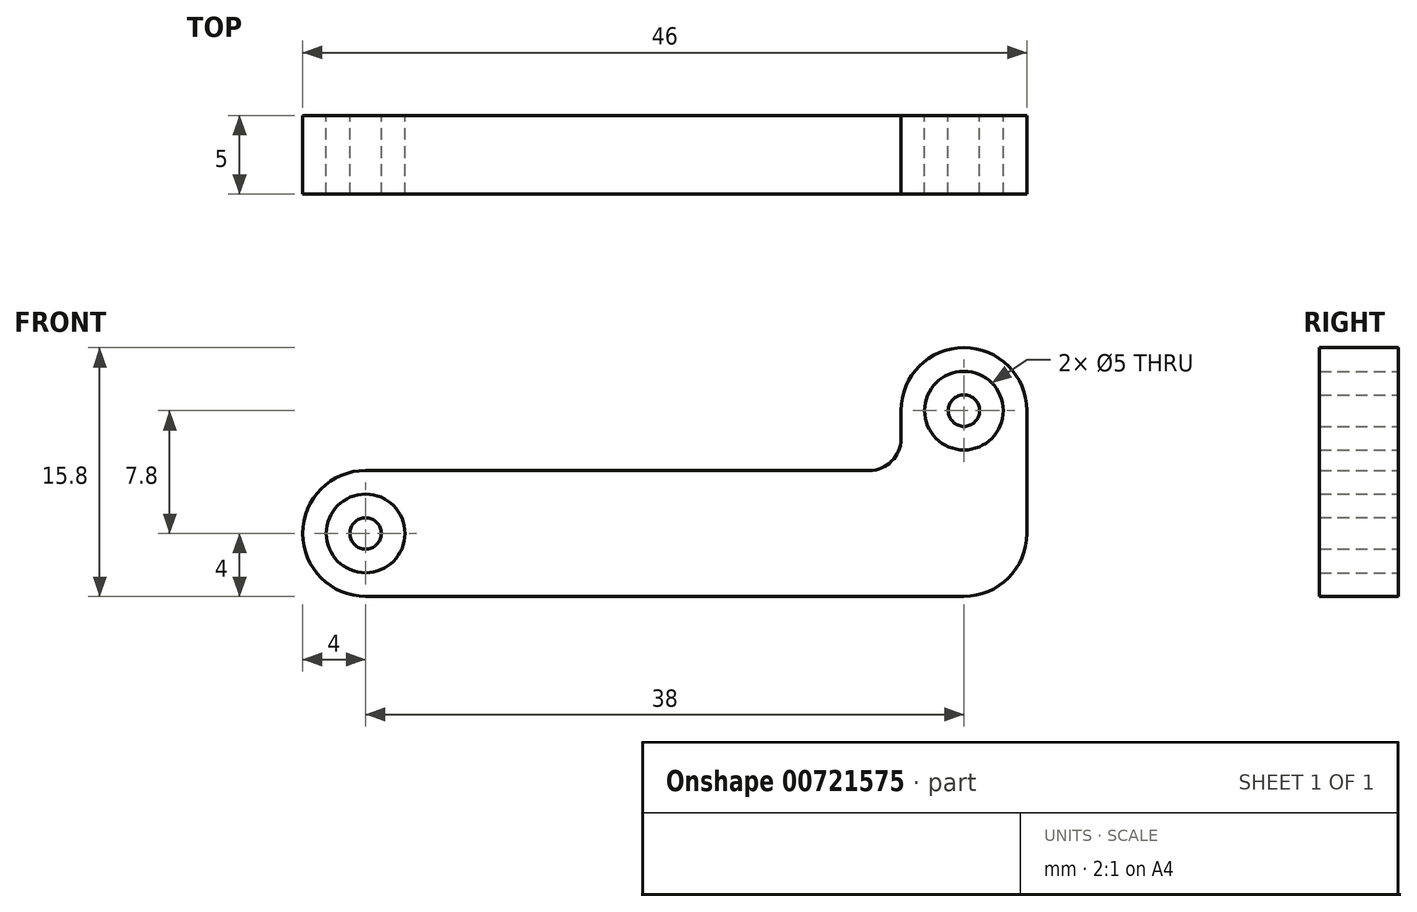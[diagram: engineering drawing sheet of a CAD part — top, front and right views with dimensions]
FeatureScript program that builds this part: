
annotation { "Feature Type Name" : "Feature", "Feature Type Description" : "" }
export const myFeature = defineFeature(function(context is Context, id is Id, definition is map)
    precondition{}
    {
        {
            var Q0;
            Q0=qCreatedBy(makeId("Front.planeOp"),FACE);
            var sketch = newSketch(context, id + "F0", { "sketchPlane" : qUnion([Q0])});
            skLineSegment(sketch, "E0.bottom", {"start": v(11, 4) * mm, "end": v(-21, 4) * mm});
            skLineSegment(sketch, "E0.top", {"start": v(17, -4) * mm, "end": v(-21, -4) * mm});
            skLineSegment(sketch, "E0.left", {"start": v(21, 7.8) * mm, "end": v(21, 0) * mm});
            skPoint(sketch, "E0.middle", {"position": v(0, 0) * mm});
            skArc(sketch, "E1", {"start": v(-21, 4) * mm, "mid": v(-25, 0) * mm, "end": v(-21, -4) * mm});
            skPoint(sketch, "E2.visualSharp", {"position": v(21, -4) * mm});
            skArc(sketch, "E2.filletArc", {"start": v(17, -4) * mm, "mid": v(19.83, -2.83) * mm, "end": v(21, 0) * mm});
            skPoint(sketch, "E3.visualSharp", {"position": v(13.9, 4) * mm});
            skArc(sketch, "E3.filletArc", {"start": v(11, 4) * mm, "mid": v(12.41, 4.59) * mm, "end": v(13, 6) * mm});
            skLineSegment(sketch, "E4", {"start": v(13, 6) * mm, "end": v(13, 7.8) * mm});
            skArc(sketch, "E5", {"start": v(21, 7.8) * mm, "mid": v(17, 11.8) * mm, "end": v(13, 7.8) * mm});
            skCircle(sketch, "E6", {"center": v(-21, 0) * mm, "radius": 2.5 * mm});
            skCircle(sketch, "E7", {"center": v(17, 7.8) * mm, "radius": 2.5 * mm});
            skCircle(sketch, "E8", {"center": v(17, 7.8) * mm, "radius": 1 * mm});
            skCircle(sketch, "E9", {"center": v(-21, 0) * mm, "radius": 1 * mm});
            skSolve(sketch);
        }
        {
            var Q0;
            Q0 = qSketchRegion(id + "F0", true);
            var Q1;
            Q1=makeQuery(id+"F0.imprint","IMPRINT",FACE,{"disambiguationData":[TD([[makeQuery(id+"F0.imprint","IMPRINT",EDGE,{"derivedFrom":sQuery(id+"F0.wireOp",EDGE,"E9")}),1.0]])]});
            var Q2;
            Q2=makeQuery(id+"F0.imprint","IMPRINT",FACE,{"disambiguationData":[TD([[makeQuery(id+"F0.imprint","IMPRINT",EDGE,{"derivedFrom":sQuery(id+"F0.wireOp",EDGE,"E8")}),1.0]])]});
            extrude(context, id + "F1", {"entities" : qUnion([Q0, Q1, Q2]), "endBound" : BoundingType.SYMMETRIC, "depth" : 5 * mm, "offsetDistance" : 25.4 * mm});
        }
    });
